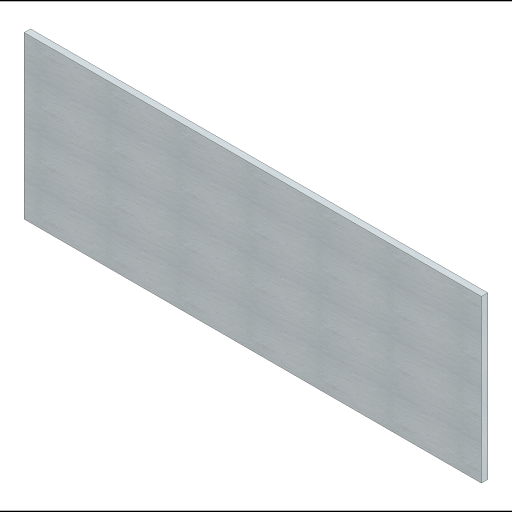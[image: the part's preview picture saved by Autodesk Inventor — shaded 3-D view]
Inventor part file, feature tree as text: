
AUTODESK INVENTOR PART (.ipt)
format: ipt  version: 2023 (Build 270158000, 158)  size: 251,904 bytes
history: native  units: in
note: dims shown in document units (in); Inventor stores cm internally (conversion verified against a paired STEP export)
features: extrude x1, sketch x1
ambient origin geometry x8: Origin, YZ Plane, XZ Plane, XY Plane, X Axis, Y Axis, Z Axis, Center Point
bodies: Solid1 (feature_tree)
feature tree (2):
  extrude  "Extrusion1"  Depth=33.94in
  sketch  "Sketch1"  dims[d0=12.0in d1=33.94in d2=0.47in d3=0.0in]
